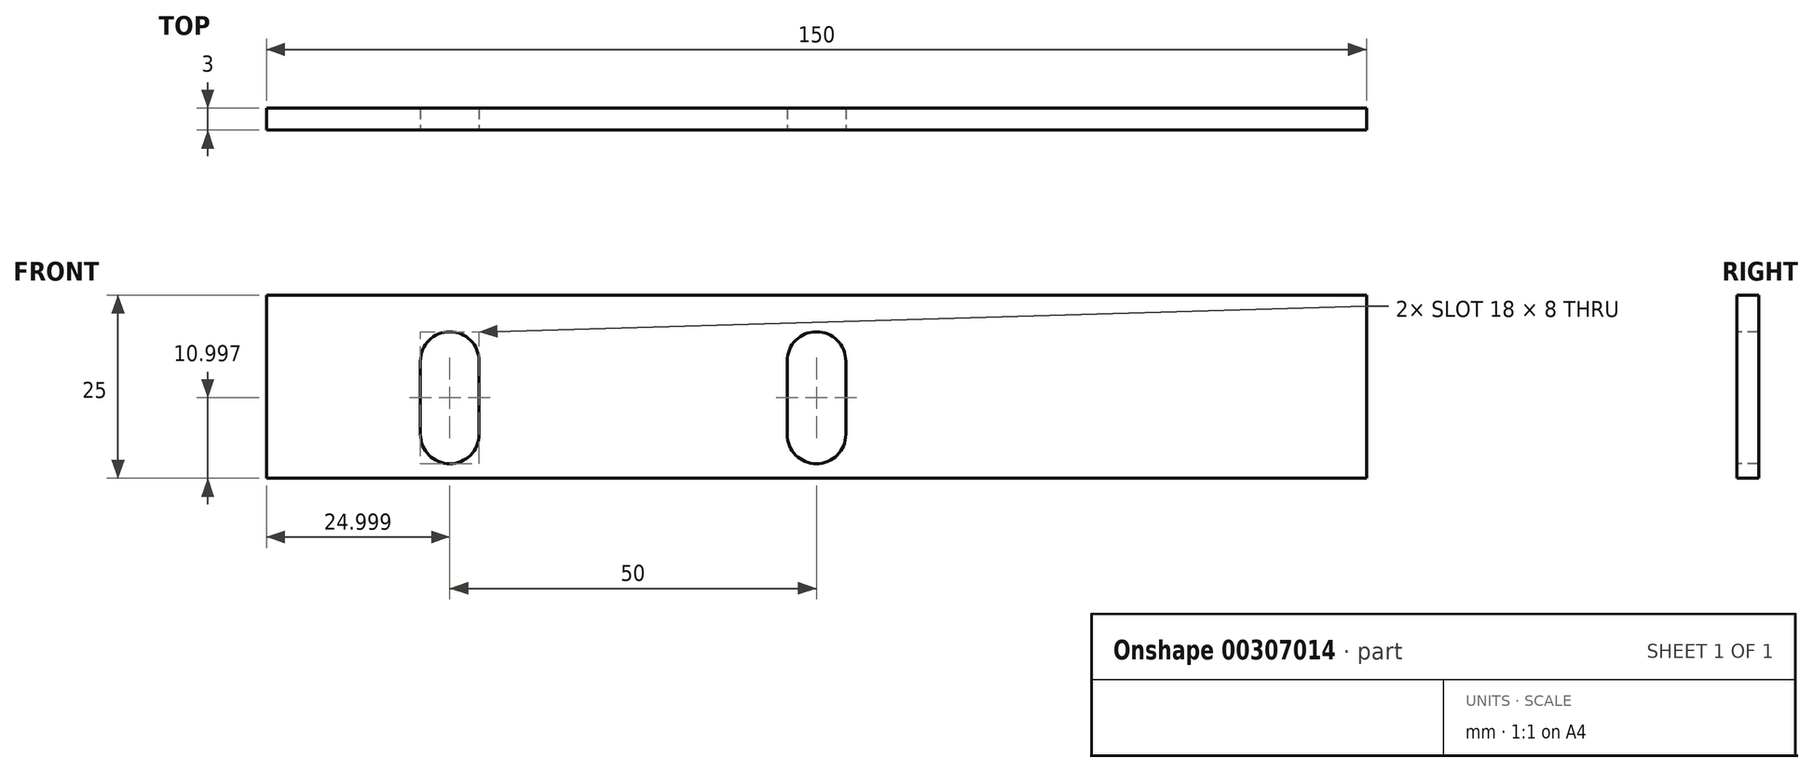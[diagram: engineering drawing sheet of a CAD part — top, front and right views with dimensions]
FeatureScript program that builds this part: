
annotation { "Feature Type Name" : "Feature", "Feature Type Description" : "" }
export const myFeature = defineFeature(function(context is Context, id is Id, definition is map)
    precondition{}
    {
        {
            var Q0;
            Q0=qCreatedBy(makeId("Front.planeOp"),FACE);
            var sketch = newSketch(context, id + "F0", { "sketchPlane" : qUnion([Q0])});
            skLineSegment(sketch, "E0.bottom", {"start": v(-74.98, -54.56) * mm, "end": v(75.02, -54.56) * mm});
            skLineSegment(sketch, "E0.top", {"start": v(-74.98, -79.56) * mm, "end": v(75.02, -79.56) * mm});
            skLineSegment(sketch, "E0.left", {"start": v(-74.98, -54.56) * mm, "end": v(-74.98, -79.56) * mm});
            skLineSegment(sketch, "E0.right", {"start": v(75.02, -54.56) * mm, "end": v(75.02, -79.56) * mm});
            skSolve(sketch);
        }
        {
            var Q0;
            Q0 = qSketchRegion(id + "F0", true);
            extrude(context, id + "F1", {"entities" : qUnion([Q0]), "depth" : 3 * mm});
        }
        {
            var Q0;
            Q0=makeQuery(id+"F1.opExtrude","CAP_FACE",FACE,{"disambiguationData":[OSD([sQuery(id+"F0.wireOp",EDGE,"E0.bottom"),sQuery(id+"F0.wireOp",EDGE,"E0.top"),sQuery(id+"F0.wireOp",EDGE,"E0.left"),sQuery(id+"F0.wireOp",EDGE,"E0.right")])],"isStart":false});
            var sketch = newSketch(context, id + "F2", { "sketchPlane" : qUnion([Q0])});
            skArc(sketch, "E1", {"start": v(-45.98, -63.56) * mm, "mid": v(-49.98, -59.56) * mm, "end": v(-53.98, -63.56) * mm});
            skLineSegment(sketch, "E2", {"start": v(-53.98, -63.56) * mm, "end": v(-53.98, -73.56) * mm});
            skLineSegment(sketch, "E3", {"start": v(-45.98, -63.56) * mm, "end": v(-45.98, -73.56) * mm});
            skArc(sketch, "E4", {"start": v(-45.98, -73.56) * mm, "mid": v(-49.98, -77.56) * mm, "end": v(-53.98, -73.56) * mm});
            skArc(sketch, "E5", {"start": v(4.02, -63.56) * mm, "mid": v(0.02, -59.56) * mm, "end": v(-3.98, -63.56) * mm});
            skLineSegment(sketch, "E6", {"start": v(-3.98, -63.56) * mm, "end": v(-3.98, -73.56) * mm});
            skLineSegment(sketch, "E7", {"start": v(4.02, -63.56) * mm, "end": v(4.02, -73.56) * mm});
            skArc(sketch, "E8", {"start": v(-3.98, -73.56) * mm, "mid": v(0.02, -77.56) * mm, "end": v(4.02, -73.56) * mm});
            skSolve(sketch);
        }
        {
            var Q0;
            Q0 = qSketchRegion(id + "F2", true);
            extrude(context, id + "F3", {"entities" : qUnion([Q0]), "operationType" : NewBodyOperationType.REMOVE, "oppositeDirection" : true, "depth" : 25 * mm});
        }
    });
